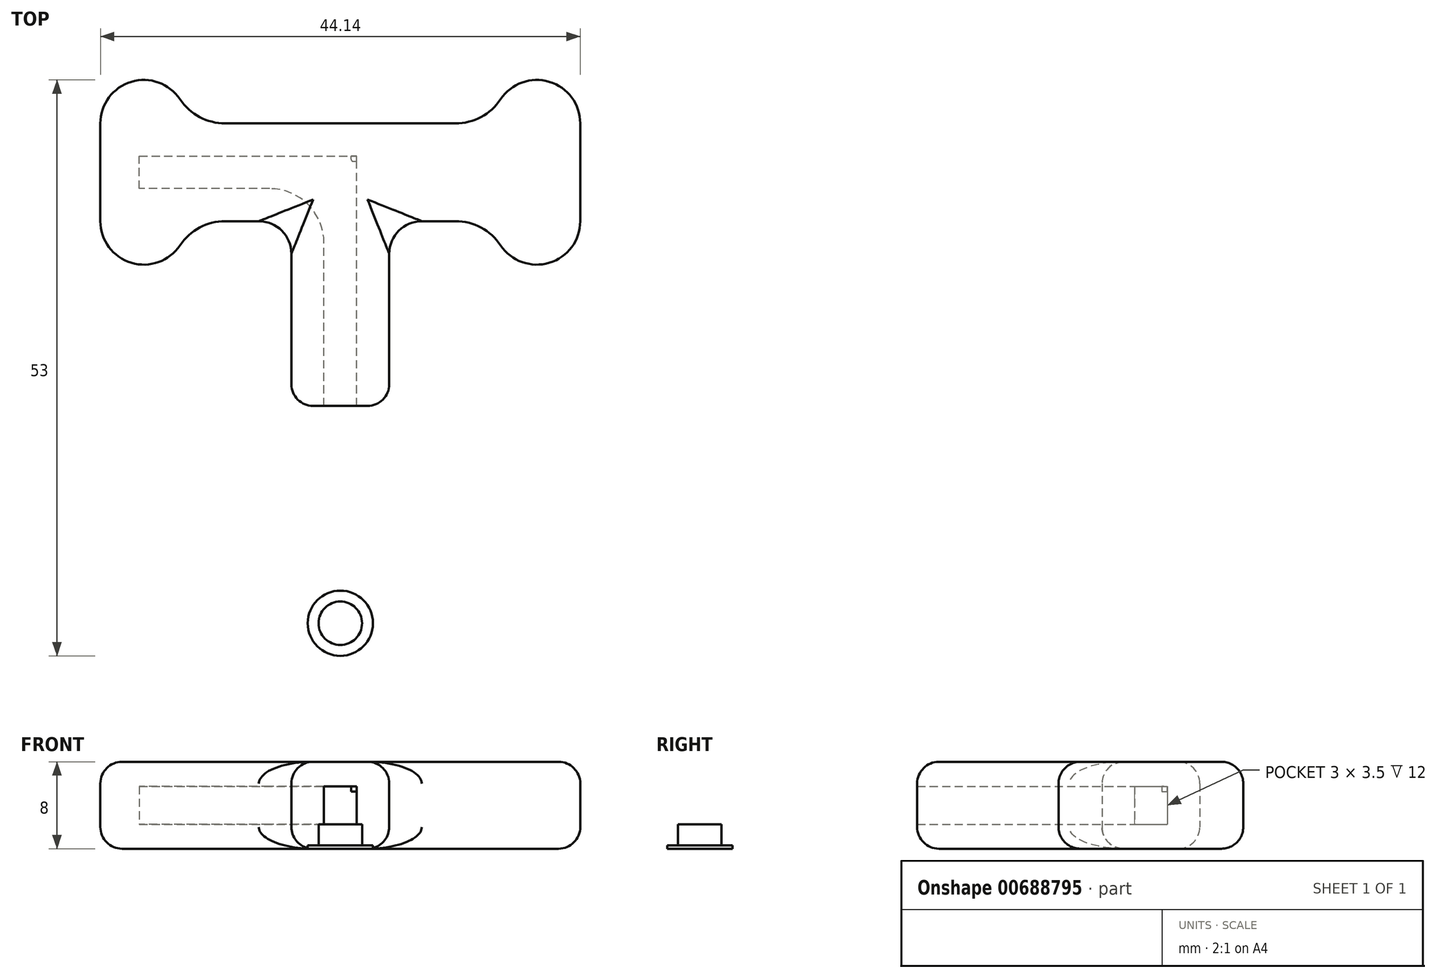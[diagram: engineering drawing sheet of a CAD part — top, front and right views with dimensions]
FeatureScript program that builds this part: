
annotation { "Feature Type Name" : "Feature", "Feature Type Description" : "" }
export const myFeature = defineFeature(function(context is Context, id is Id, definition is map)
    precondition{}
    {
        {
            var Q0;
            Q0=qCreatedBy(makeId("Top.planeOp"),FACE);
            var sketch = newSketch(context, id + "F0", { "sketchPlane" : qUnion([Q0])});
            skPoint(sketch, "E0.middle", {"position": v(0, 0) * mm});
            skLineSegment(sketch, "E1", {"start": v(6, -15) * mm, "end": v(9, -15) * mm});
            skLineSegment(sketch, "E2", {"start": v(6, -15) * mm, "end": v(6, 5) * mm});
            skLineSegment(sketch, "E3", {"start": v(6, 5) * mm, "end": v(-11, 5) * mm});
            skLineSegment(sketch, "E4", {"start": v(-11, 5) * mm, "end": v(-11, 8) * mm});
            skLineSegment(sketch, "E5", {"start": v(-11, 8) * mm, "end": v(9, 8) * mm});
            skLineSegment(sketch, "E6", {"start": v(9, -15) * mm, "end": v(9, 8) * mm});
            skLineSegment(sketch, "E7", {"start": v(12, -15) * mm, "end": v(12, 2) * mm});
            skLineSegment(sketch, "E8", {"start": v(12, 11) * mm, "end": v(7.5, 11) * mm});
            skLineSegment(sketch, "E9", {"start": v(-3.1, 2) * mm, "end": v(3, 2) * mm});
            skLineSegment(sketch, "E10", {"start": v(3, 2) * mm, "end": v(3, -15) * mm});
            skLineSegment(sketch, "E11", {"start": v(3, -15) * mm, "end": v(6, -15) * mm});
            skLineSegment(sketch, "E12", {"start": v(9, -15) * mm, "end": v(12, -15) * mm});
            skArc(sketch, "E13", {"start": v(-14.57, 2) * mm, "mid": v(-11.74, -1.83) * mm, "end": v(-7.25, -0.22) * mm});
            skPoint(sketch, "E14.newPointA", {"position": v(-6.57, 2) * mm});
            skPoint(sketch, "E14.newPointB", {"position": v(-14.57, 2) * mm});
            skArc(sketch, "E14.filletArc", {"start": v(-3.1, 2) * mm, "mid": v(-5.45, 1.4) * mm, "end": v(-7.25, -0.22) * mm});
            skLineSegment(sketch, "E15", {"start": v(7.5, -15) * mm, "end": v(7.5, 11) * mm, "construction": true});
            skLineSegment(sketch, "E16", {"start": v(7.5, 11) * mm, "end": v(-1.63, 11) * mm});
            skLineSegment(sketch, "E17", {"start": v(-14.57, 2) * mm, "end": v(-14.57, 11) * mm});
            skArc(sketch, "E18", {"start": v(-7.25, 13.22) * mm, "mid": v(-11.74, 14.83) * mm, "end": v(-14.57, 11) * mm});
            skLineSegment(sketch, "E19", {"start": v(-1.63, 11) * mm, "end": v(-3.1, 11) * mm});
            skPoint(sketch, "E20.visualSharp", {"position": v(-6.57, 11) * mm});
            skArc(sketch, "E20.filletArc", {"start": v(-7.25, 13.22) * mm, "mid": v(-5.45, 11.6) * mm, "end": v(-3.1, 11) * mm});
            skLineSegment(sketch, "E21.MirrorCS", {"start": v(7.5, 11) * mm, "end": v(16.63, 11) * mm});
            skArc(sketch, "E22.MirrorCS", {"start": v(22.25, 13.22) * mm, "mid": v(26.74, 14.83) * mm, "end": v(29.57, 11) * mm});
            skArc(sketch, "E23.MirrorCS", {"start": v(22.25, 13.22) * mm, "mid": v(20.45, 11.6) * mm, "end": v(18.1, 11) * mm});
            skLineSegment(sketch, "E24.MirrorCS", {"start": v(16.63, 11) * mm, "end": v(18.1, 11) * mm});
            skLineSegment(sketch, "E25.MirrorCS", {"start": v(29.57, 2) * mm, "end": v(29.57, 11) * mm});
            skLineSegment(sketch, "E26.MirrorCS", {"start": v(18.1, 2) * mm, "end": v(12, 2) * mm});
            skArc(sketch, "E27.MirrorCS", {"start": v(18.1, 2) * mm, "mid": v(20.45, 1.4) * mm, "end": v(22.25, -0.22) * mm});
            skArc(sketch, "E28.MirrorCS", {"start": v(29.57, 2) * mm, "mid": v(26.74, -1.83) * mm, "end": v(22.25, -0.22) * mm});
            skCircle(sketch, "E29", {"center": v(7.5, -35) * mm, "radius": 3 * mm});
            skCircle(sketch, "E30", {"center": v(7.5, -35) * mm, "radius": 2 * mm});
            skSolve(sketch);
        }
        {
            var Q0;
            {var subQ1=sQuery(id+"F0.wireOp",EDGE,"E0.bottom");Q0=makeQuery(id+"F0.imprint","IMPRINT",FACE,{"disambiguationData":[TD([[makeQuery(id+"F0.imprint","IMPRINT",EDGE,{"derivedFrom":subQ1}),1.0]])]});}
            var Q1;
            Q1=makeQuery(id+"F0.imprint","IMPRINT",FACE,{"disambiguationData":[TD([[makeQuery(id+"F0.imprint","IMPRINT",EDGE,{"derivedFrom":sQuery(id+"F0.wireOp",EDGE,"E2")}),1.0]])]});
            extrude(context, id + "F1", {"entities" : qUnion([Q0, Q1]), "depth" : (2.25 + 2.25 + 3.5) * mm, "offsetDistance" : 25 * mm});
        }
        {
            var Q0;
            Q0=makeQuery(id+"F0.imprint","IMPRINT",FACE,{"disambiguationData":[TD([[makeQuery(id+"F0.imprint","IMPRINT",EDGE,{"derivedFrom":sQuery(id+"F0.wireOp",EDGE,"E1")}),1.0]])]});
            var Q1;
            Q1=makeQuery(id+"F0.imprint","IMPRINT",FACE,{"disambiguationData":[TD([[makeQuery(id+"F0.imprint","IMPRINT",EDGE,{"derivedFrom":sQuery(id+"F0.wireOp",EDGE,"LMaaSgrv-SqUP-iJYc-fxXf-p2NaT9bKtcqD")}),1.0]])]});
            var Q2;
            Q2=makeQuery(id+"F0.imprint","IMPRINT",FACE,{"disambiguationData":[TD([[makeQuery(id+"F0.imprint","IMPRINT",EDGE,{"derivedFrom":sQuery(id+"F0.wireOp",EDGE,"E30")}),1.0]])]});
            extrude(context, id + "F2", {"entities" : qUnion([Q0, Q1, Q2]), "operationType" : NewBodyOperationType.ADD, "depth" : 2.25 * mm, "offsetDistance" : 25 * mm});
        }
        {
            var Q0;
            Q0=makeQuery(id+"F0.imprint","IMPRINT",FACE,{"disambiguationData":[TD([[makeQuery(id+"F0.imprint","IMPRINT",EDGE,{"derivedFrom":sQuery(id+"F0.wireOp",EDGE,"E1")}),1.0]])]});
            extrude(context, id + "F3", {"entities" : qUnion([Q0]), "operationType" : NewBodyOperationType.ADD, "depth" : 8 * mm, "offsetDistance" : 25 * mm, "hasSecondDirection" : true, "secondDirectionOppositeDirection" : false, "secondDirectionDepth" : (2.25 + 3.5) * mm});
        }
        {
            var Q0;
            {var subQ0=sQuery(id+"F0.wireOp",EDGE,"E6");var subQ1=sQuery(id+"F0.wireOp",EDGE,"E5");var subQ2=sQuery(id+"F0.wireOp",EDGE,"E4");var subQ3=sQuery(id+"F0.wireOp",EDGE,"E3");var subQ4=sQuery(id+"F0.wireOp",EDGE,"E2");Q0=makeQuery(id+"F3.boolean.opBoolean","MERGE",FACE,{"derivedFrom":[makeQuery(id+"F1.opExtrude","CAP_FACE",FACE,{"disambiguationData":[OSD([subQ4,subQ3,subQ2,subQ1,subQ0,sQuery(id+"F0.wireOp",EDGE,"E7"),sQuery(id+"F0.wireOp",EDGE,"E9"),sQuery(id+"F0.wireOp",EDGE,"E10"),sQuery(id+"F0.wireOp",EDGE,"E11"),sQuery(id+"F0.wireOp",EDGE,"E12"),sQuery(id+"F0.wireOp",EDGE,"E13"),sQuery(id+"F0.wireOp",EDGE,"E14.filletArc"),sQuery(id+"F0.wireOp",EDGE,"E16"),sQuery(id+"F0.wireOp",EDGE,"E17"),sQuery(id+"F0.wireOp",EDGE,"E18"),sQuery(id+"F0.wireOp",EDGE,"E19"),sQuery(id+"F0.wireOp",EDGE,"E20.filletArc"),sQuery(id+"F0.wireOp",EDGE,"E21.MirrorCS"),sQuery(id+"F0.wireOp",EDGE,"E22.MirrorCS"),sQuery(id+"F0.wireOp",EDGE,"E23.MirrorCS"),sQuery(id+"F0.wireOp",EDGE,"E24.MirrorCS"),sQuery(id+"F0.wireOp",EDGE,"E25.MirrorCS"),sQuery(id+"F0.wireOp",EDGE,"E26.MirrorCS"),sQuery(id+"F0.wireOp",EDGE,"E27.MirrorCS"),sQuery(id+"F0.wireOp",EDGE,"E28.MirrorCS")])],"isStart":false}),makeQuery(id+"F3.opExtrude","CAP_FACE",FACE,{"disambiguationData":[OSD([sQuery(id+"F0.wireOp",EDGE,"E1"),subQ4,subQ3,subQ2,subQ1,subQ0])],"isStart":false})]});}
            fillet(context, id + "F4", {"entities" : qUnion([Q0]), "radius" : 2 * mm, "tangentPropagation" : true, "allowEdgeOverflow" : false});
        }
        {
            var Q0;
            {var subQ0=sQuery(id+"F0.wireOp",EDGE,"E6");var subQ1=sQuery(id+"F0.wireOp",EDGE,"E5");var subQ2=sQuery(id+"F0.wireOp",EDGE,"E4");var subQ3=sQuery(id+"F0.wireOp",EDGE,"E3");var subQ4=sQuery(id+"F0.wireOp",EDGE,"E2");Q0=makeQuery(id+"F2.boolean.opBoolean","MERGE",FACE,{"derivedFrom":[makeQuery(id+"F1.opExtrude","CAP_FACE",FACE,{"disambiguationData":[OSD([subQ4,subQ3,subQ2,subQ1,subQ0,sQuery(id+"F0.wireOp",EDGE,"E7"),sQuery(id+"F0.wireOp",EDGE,"E9"),sQuery(id+"F0.wireOp",EDGE,"E10"),sQuery(id+"F0.wireOp",EDGE,"E11"),sQuery(id+"F0.wireOp",EDGE,"E12"),sQuery(id+"F0.wireOp",EDGE,"E13"),sQuery(id+"F0.wireOp",EDGE,"E14.filletArc"),sQuery(id+"F0.wireOp",EDGE,"E16"),sQuery(id+"F0.wireOp",EDGE,"E17"),sQuery(id+"F0.wireOp",EDGE,"E18"),sQuery(id+"F0.wireOp",EDGE,"E19"),sQuery(id+"F0.wireOp",EDGE,"E20.filletArc"),sQuery(id+"F0.wireOp",EDGE,"E21.MirrorCS"),sQuery(id+"F0.wireOp",EDGE,"E22.MirrorCS"),sQuery(id+"F0.wireOp",EDGE,"E23.MirrorCS"),sQuery(id+"F0.wireOp",EDGE,"E24.MirrorCS"),sQuery(id+"F0.wireOp",EDGE,"E25.MirrorCS"),sQuery(id+"F0.wireOp",EDGE,"E26.MirrorCS"),sQuery(id+"F0.wireOp",EDGE,"E27.MirrorCS"),sQuery(id+"F0.wireOp",EDGE,"E28.MirrorCS")])],"isStart":true}),makeQuery(id+"F2.opExtrude","CAP_FACE",FACE,{"disambiguationData":[OSD([sQuery(id+"F0.wireOp",EDGE,"E1"),subQ4,subQ3,subQ2,subQ1,subQ0])],"isStart":true})]});}
            fillet(context, id + "F5", {"entities" : qUnion([Q0]), "radius" : 2 * mm, "tangentPropagation" : true, "allowEdgeOverflow" : false});
        }
        {
            var Q0;
            Q0=makeQuery(id+"F1.opExtrude","SWEPT_EDGE",EDGE,{"disambiguationData":[OSD([sQuery(id+"F0.wireOp",EDGE,"E10"),sQuery(id+"F0.wireOp",EDGE,"E11")])]});
            var Q1;
            Q1=makeQuery(id+"F1.opExtrude","SWEPT_EDGE",EDGE,{"disambiguationData":[OSD([sQuery(id+"F0.wireOp",EDGE,"E7"),sQuery(id+"F0.wireOp",EDGE,"E12")])]});
            fillet(context, id + "F6", {"entities" : qUnion([Q0, Q1]), "radius" : 2 * mm, "tangentPropagation" : true, "allowEdgeOverflow" : false});
        }
        {
            var Q0;
            Q0=makeQuery(id+"F1.opExtrude","SWEPT_EDGE",EDGE,{"disambiguationData":[OSD([sQuery(id+"F0.wireOp",EDGE,"E2"),sQuery(id+"F0.wireOp",EDGE,"E3")])]});
            fillet(context, id + "F7", {"entities" : qUnion([Q0]), "radius" : 5 * mm, "tangentPropagation" : true, "allowEdgeOverflow" : false});
        }
        {
            var Q0;
            Q0=makeQuery(id+"F1.opExtrude","SWEPT_EDGE",EDGE,{"disambiguationData":[OSD([sQuery(id+"F0.wireOp",EDGE,"E9"),sQuery(id+"F0.wireOp",EDGE,"E10")])]});
            var Q1;
            Q1=makeQuery(id+"F1.opExtrude","SWEPT_EDGE",EDGE,{"disambiguationData":[OSD([sQuery(id+"F0.wireOp",EDGE,"E7"),sQuery(id+"F0.wireOp",EDGE,"E26.MirrorCS")])]});
            fillet(context, id + "F8", {"entities" : qUnion([Q0, Q1]), "radius" : 3 * mm, "tangentPropagation" : true, "allowEdgeOverflow" : false});
        }
        {
            var Q0;
            Q0=makeQuery(id+"F1.opExtrude","SWEPT_FACE",FACE,{"disambiguationData":[OSD([sQuery(id+"F0.wireOp",EDGE,"E5")])]});
            var sketch = newSketch(context, id + "F9", { "sketchPlane" : qUnion([Q0])});
            skLineSegment(sketch, "E31", {"start": v(9, 5.75) * mm, "end": v(9, 5.25) * mm});
            skLineSegment(sketch, "E32", {"start": v(9, 5.25) * mm, "end": v(8.5, 5.25) * mm});
            skLineSegment(sketch, "E33", {"start": v(8.5, 5.25) * mm, "end": v(8.5, 5.75) * mm});
            skSolve(sketch);
        }
        {
            var Q0;
            {var subQ0=sQuery(id+"F9.wireOp",EDGE,"E31");Q0=makeQuery(id+"F9.imprint","IMPRINT",FACE,{"disambiguationData":[TD([[makeQuery(id+"F9.imprint","IMPRINT",EDGE,{"derivedFrom":subQ0}),-1.0]])]});}
            extrude(context, id + "F10", {"entities" : qUnion([Q0]), "operationType" : NewBodyOperationType.ADD, "depth" : .5 * mm, "offsetDistance" : 25 * mm});
        }
        {
            var Q0;
            Q0=makeQuery(id+"F10.opExtrude","CAP_EDGE",EDGE,{"disambiguationData":[OSD([sQuery(id+"F9.wireOp",EDGE,"E33")])],"isStart":false});
            var Q1;
            Q1=makeQuery(id+"F10.opExtrude","CAP_EDGE",EDGE,{"disambiguationData":[OSD([sQuery(id+"F9.wireOp",EDGE,"E31")])],"isStart":false});
            var Q2;
            Q2=makeQuery(id+"F10.opExtrude","CAP_EDGE",EDGE,{"disambiguationData":[OSD([sQuery(id+"F9.wireOp",EDGE,"E33")])],"isStart":true});
            fillet(context, id + "F11", {"entities" : qUnion([Q0, Q1, Q2]), "radius" : .2 * mm, "tangentPropagation" : true, "allowEdgeOverflow" : false});
        }
        {
            var Q0;
            Q0=makeQuery(id+"F0.imprint","IMPRINT",FACE,{"disambiguationData":[TD([[makeQuery(id+"F0.imprint","IMPRINT",EDGE,{"derivedFrom":sQuery(id+"F0.wireOp",EDGE,"E29")}),1.0]])]});
            extrude(context, id + "F12", {"entities" : qUnion([Q0]), "operationType" : NewBodyOperationType.ADD, "depth" : 0.3 * mm, "offsetDistance" : 25 * mm});
        }
    });
